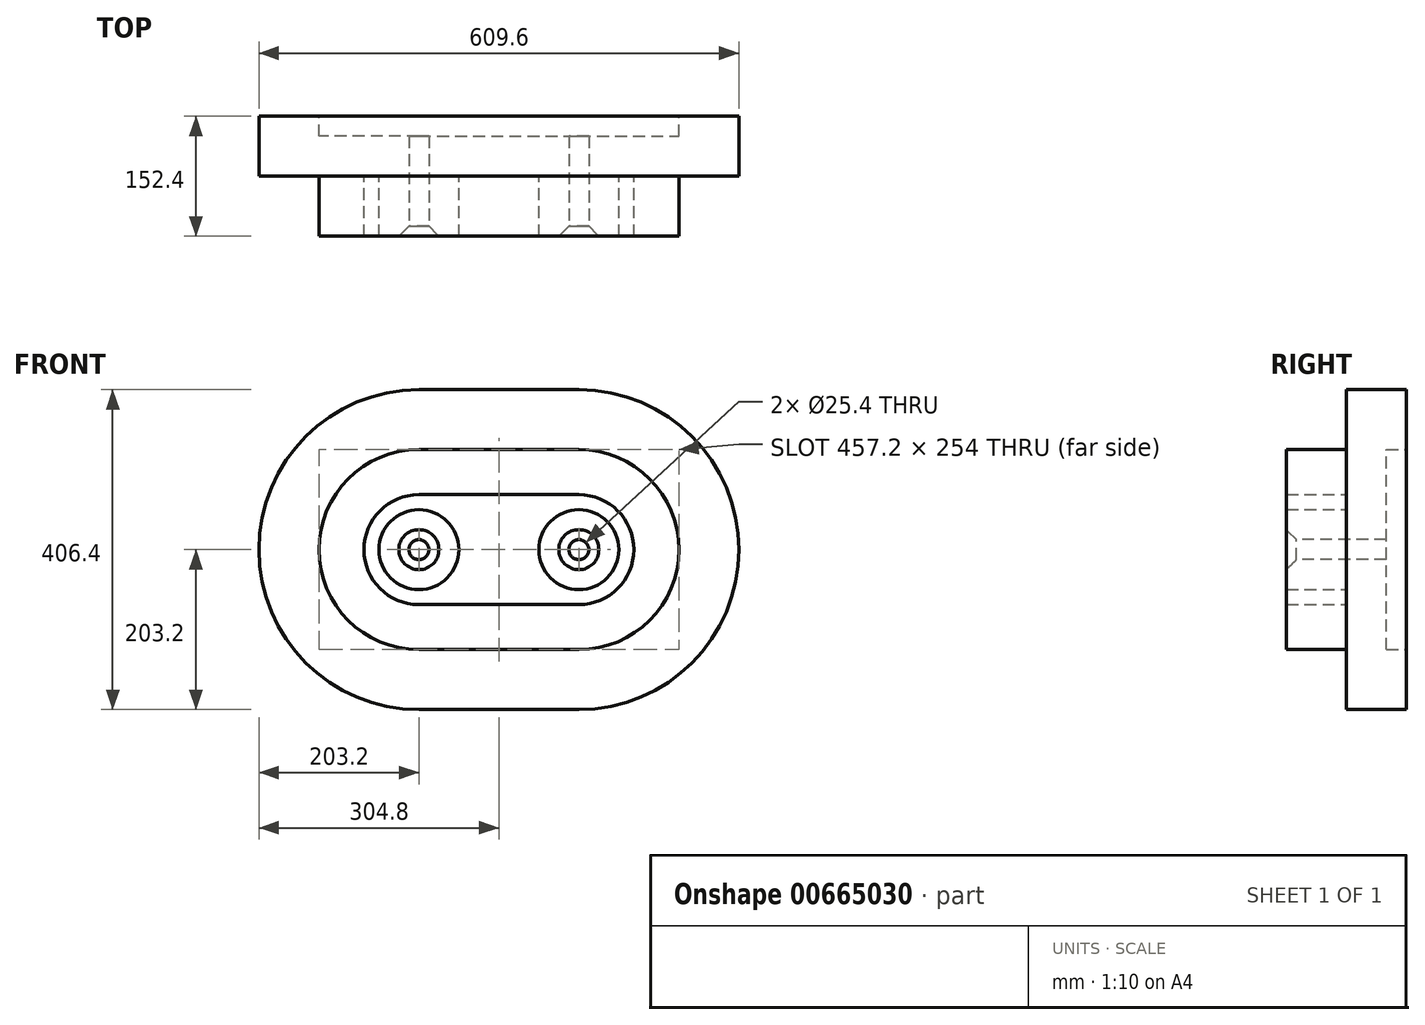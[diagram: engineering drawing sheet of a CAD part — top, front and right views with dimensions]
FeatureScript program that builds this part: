
annotation { "Feature Type Name" : "Feature", "Feature Type Description" : "" }
export const myFeature = defineFeature(function(context is Context, id is Id, definition is map)
    precondition{}
    {
        {
            var Q0;
            Q0=qCreatedBy(makeId("Front.planeOp"),FACE);
            var sketch = newSketch(context, id + "F0", { "sketchPlane" : qUnion([Q0])});
            skLineSegment(sketch, "E0", {"start": v(203.2, 0) * mm, "end": v(406.4, 0) * mm});
            skLineSegment(sketch, "E1", {"start": v(406.4, 406.4) * mm, "end": v(203.2, 406.4) * mm});
            skArc(sketch, "E2", {"start": v(406.4, 0) * mm, "mid": v(550.08, 59.52) * mm, "end": v(609.6, 203.2) * mm});
            skArc(sketch, "E3", {"start": v(406.4, 406.4) * mm, "mid": v(550.08, 346.88) * mm, "end": v(609.6, 203.2) * mm});
            skArc(sketch, "E4", {"start": v(203.2, 0) * mm, "mid": v(59.52, 59.52) * mm, "end": v(0, 203.2) * mm});
            skArc(sketch, "E5", {"start": v(203.2, 406.4) * mm, "mid": v(59.52, 346.88) * mm, "end": v(0, 203.2) * mm});
            skLineSegment(sketch, "E6.0", {"start": v(406.4, 330.2) * mm, "end": v(203.2, 330.2) * mm});
            skLineSegment(sketch, "E7.0", {"start": v(203.2, 76.2) * mm, "end": v(406.4, 76.2) * mm});
            skArc(sketch, "E8", {"start": v(406.4, 76.2) * mm, "mid": v(533.4, 203.2) * mm, "end": v(406.4, 330.2) * mm});
            skArc(sketch, "E9", {"start": v(203.2, 76.2) * mm, "mid": v(76.2, 203.2) * mm, "end": v(203.2, 330.2) * mm});
            skCircle(sketch, "E10", {"center": v(203.2, 203.2) * mm, "radius": 50.8 * mm});
            skCircle(sketch, "E11", {"center": v(406.4, 203.2) * mm, "radius": 50.8 * mm});
            skLineSegment(sketch, "E12.0", {"start": v(406.4, 304.8) * mm, "end": v(203.2, 304.8) * mm});
            skLineSegment(sketch, "E13.0", {"start": v(203.2, 101.6) * mm, "end": v(406.4, 101.6) * mm});
            skLineSegment(sketch, "E14.0", {"start": v(203.2, 133.35) * mm, "end": v(406.4, 133.35) * mm});
            skLineSegment(sketch, "E15.0", {"start": v(406.4, 273.05) * mm, "end": v(203.2, 273.05) * mm});
            skArc(sketch, "E16", {"start": v(203.2, 304.8) * mm, "mid": v(101.6, 203.2) * mm, "end": v(203.2, 101.6) * mm});
            skArc(sketch, "E17", {"start": v(203.2, 273.05) * mm, "mid": v(133.35, 203.2) * mm, "end": v(203.2, 133.35) * mm});
            skArc(sketch, "E18", {"start": v(406.4, 273.05) * mm, "mid": v(476.25, 203.2) * mm, "end": v(406.4, 133.35) * mm});
            skArc(sketch, "E19", {"start": v(406.4, 304.8) * mm, "mid": v(508, 203.2) * mm, "end": v(406.4, 101.6) * mm});
            skCircle(sketch, "E20", {"center": v(203.2, 203.2) * mm, "radius": 25.4 * mm});
            skCircle(sketch, "E21", {"center": v(203.2, 203.2) * mm, "radius": 12.7 * mm});
            skCircle(sketch, "E22", {"center": v(406.4, 203.2) * mm, "radius": 25.4 * mm});
            skCircle(sketch, "E23", {"center": v(406.4, 203.2) * mm, "radius": 12.7 * mm});
            skSolve(sketch);
        }
        {
            var Q0;
            Q0=makeQuery(id+"F0.imprint","IMPRINT",FACE,{"disambiguationData":[TD([[makeQuery(id+"F0.imprint","IMPRINT",EDGE,{"derivedFrom":sQuery(id+"F0.wireOp",EDGE,"E0")}),1.0]])]});
            extrude(context, id + "F1", {"entities" : qUnion([Q0]), "depth" : 76.2 * mm, "offsetDistance" : 25.4 * mm});
        }
        {
            var Q0;
            Q0=makeQuery(id+"F0.imprint","IMPRINT",FACE,{"disambiguationData":[TD([[makeQuery(id+"F0.imprint","IMPRINT",EDGE,{"derivedFrom":sQuery(id+"F0.wireOp",EDGE,"E6.0")}),1.0]])]});
            var Q1;
            Q1=makeQuery(id+"F0.imprint","IMPRINT",FACE,{"disambiguationData":[TD([[makeQuery(id+"F0.imprint","IMPRINT",EDGE,{"derivedFrom":sQuery(id+"F0.wireOp",EDGE,"E12.0")}),1.0]])]});
            extrude(context, id + "F2", {"entities" : qUnion([Q0, Q1]), "operationType" : NewBodyOperationType.ADD, "depth" : 152.4 * mm, "offsetDistance" : 25.4 * mm, "hasSecondDirection" : true, "secondDirectionOppositeDirection" : false, "secondDirectionDepth" : 25.4 * mm});
        }
        {
            var Q0;
            Q0=makeQuery(id+"F0.imprint","IMPRINT",FACE,{"disambiguationData":[TD([[makeQuery(id+"F0.imprint","IMPRINT",EDGE,{"derivedFrom":sQuery(id+"F0.wireOp",EDGE,"E10")}),-1.0]])]});
            extrude(context, id + "F3", {"entities" : qUnion([Q0]), "operationType" : NewBodyOperationType.ADD, "depth" : 76.2 * mm, "offsetDistance" : 25.4 * mm, "hasSecondDirection" : true, "secondDirectionOppositeDirection" : false, "secondDirectionDepth" : 25.4 * mm});
        }
        {
            var Q0;
            Q0=makeQuery(id+"F0.imprint","IMPRINT",FACE,{"disambiguationData":[TD([[makeQuery(id+"F0.imprint","IMPRINT",EDGE,{"derivedFrom":sQuery(id+"F0.wireOp",EDGE,"E11")}),1.0]])]});
            var Q1;
            Q1=makeQuery(id+"F0.imprint","IMPRINT",FACE,{"disambiguationData":[TD([[makeQuery(id+"F0.imprint","IMPRINT",EDGE,{"derivedFrom":sQuery(id+"F0.wireOp",EDGE,"E10")}),1.0]])]});
            var Q2;
            Q2=makeQuery(id+"F0.imprint","IMPRINT",FACE,{"disambiguationData":[TD([[makeQuery(id+"F0.imprint","IMPRINT",EDGE,{"derivedFrom":sQuery(id+"F0.wireOp",EDGE,"E20")}),1.0]])]});
            var Q3;
            Q3=makeQuery(id+"F0.imprint","IMPRINT",FACE,{"disambiguationData":[TD([[makeQuery(id+"F0.imprint","IMPRINT",EDGE,{"derivedFrom":sQuery(id+"F0.wireOp",EDGE,"E22")}),1.0]])]});
            var Q4;
            Q4=makeQuery(id+"F0.imprint","IMPRINT",FACE,{"disambiguationData":[TD([[makeQuery(id+"F0.imprint","IMPRINT",EDGE,{"derivedFrom":sQuery(id+"F0.wireOp",EDGE,"E21")}),1.0]])]});
            var Q5;
            Q5=makeQuery(id+"F0.imprint","IMPRINT",FACE,{"disambiguationData":[TD([[makeQuery(id+"F0.imprint","IMPRINT",EDGE,{"derivedFrom":sQuery(id+"F0.wireOp",EDGE,"E23")}),1.0]])]});
            extrude(context, id + "F4", {"entities" : qUnion([Q0, Q1, Q2, Q3, Q4, Q5]), "operationType" : NewBodyOperationType.ADD, "depth" : 152.4 * mm, "offsetDistance" : 25.4 * mm, "hasSecondDirection" : true, "secondDirectionOppositeDirection" : false, "secondDirectionDepth" : 25.4 * mm});
        }
        {
            var Q0;
            Q0=makeQuery(id+"F4.opExtrude","CAP_FACE",FACE,{"disambiguationData":[OSD([sQuery(id+"F0.wireOp",EDGE,"E10")])],"isStart":false});
            var sketch = newSketch(context, id + "F5", { "sketchPlane" : qUnion([Q0])});
            skLineSegment(sketch, "E24", {"start": v(254, 203.2) * mm, "end": v(406.4, 203.2) * mm});
            skLineSegment(sketch, "E25", {"start": v(254, 203.2) * mm, "end": v(203.2, 203.2) * mm});
            skSolve(sketch);
        }
        {
            var Q0;
            Q0=sQuery(id+"F5.wireOp",VERTEX,"E25.end");
            var Q1;
            Q1=sQuery(id+"F5.wireOp",VERTEX,"E24.end");
            var Q2;
            Q2=makeQuery(id+"F1.opExtrude","SWEPT_BODY",BODY,{"disambiguationData":[OSD([sQuery(id+"F0.wireOp",EDGE,"E0"),sQuery(id+"F0.wireOp",EDGE,"E1"),sQuery(id+"F0.wireOp",EDGE,"E3"),sQuery(id+"F0.wireOp",EDGE,"E4"),sQuery(id+"F0.wireOp",EDGE,"E5"),sQuery(id+"F0.wireOp",EDGE,"E2"),sQuery(id+"F0.wireOp",EDGE,"E6.0"),sQuery(id+"F0.wireOp",EDGE,"E7.0"),sQuery(id+"F0.wireOp",EDGE,"E8"),sQuery(id+"F0.wireOp",EDGE,"E9")])]});
            hole(context, id + "F6", {"style" : HoleStyle.C_SINK, "endStyle" : HoleEndStyle.THROUGH, "holeDiameter" : 25.4 * mm, "cSinkDiameter" : 50.8 * mm, "cSinkAngle" : 90 * degree, "majorDiameter" : 6.35 * mm, "isTappedThrough" : true, "tappedDepth" : 12.7 * mm, "tapClearance" : 3, "locations" : qUnion([Q0, Q1]), "scope" : qUnion([Q2])});
        }
    });
